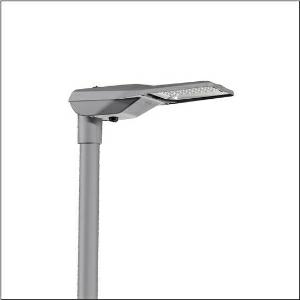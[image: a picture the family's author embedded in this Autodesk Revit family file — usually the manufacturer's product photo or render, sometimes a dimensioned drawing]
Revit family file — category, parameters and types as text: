
# Revit family: streetlight_sl_21_iq_mini___st1_0ab_5xe2m31y08gb_c9fc
name_source: partatom
category: Lighting Fixtures
units: mm (PartAtom-declared; Revit-internal decimal feet)

## family parameters
Cut with Voids When Loaded = No
Host = Face
Light Source = No
Part Type = Normal
Room Calculation Point = No
Round Connector Dimension = Use Diameter
Shared = No

## types (1)
- --- (1 x LED, 5270 lm, 39.8 W, 3000K)
    Apparent Load = 40 VA
    CIE Flux Codes = 38 73 97 100 100
    Color Rendering = 70
    Color Temperature = 3000K
    Default Elevation = 1800 mm
    Description = Streetlight SL 21 iQ mini, mast luminaire, primary light control with lens, of PMMA, primary optical cover: cover, of toughened safety glass, transparent, light distribution: ST1.0aB, light emission: direct distribution, primary light characteristic: asymmetric, installation type: post-top, side-entry, LED, High Power LED, rated luminous flux: 5.270lm, luminous efficacy: 132lm/W, light colour: 730, colour temperature: 3000K, control gear: iQ-Street Remote, D4i with power reduction, control: pre-setting: logarithmic dimming characteristic, Street-Remote, Auto-Match, Temp-Guard, Lumen-Switch, Night-Set, Smart-Wire, Light-Fading, Desk-Remote (wireless, voltage-free reading and setting of iQ features in the workshop via application-optimized NFC function/RFID function), optimised constant luminous flux control (CLO 2.0), mains connection: 220..240V, AC, 50/60Hz, start of lifetime: 40W, end of service life: 41W, reduction: 18W, luminaire housing, of diecast aluminium, powder-coated, Siteco® metallic grey (DB 702S), corrosivity category C5 mid according to DIN EN ISO 12944, please order mast flange separately, inclination adjustable: 0°, 5°, 10°, 15°, sealing non-destructively replaceable, multi-level sealing system, length: 628mm, width: 235mm, height: 110mm, mast flange for spigot size: 42mm (side-entry): 5XC10008XM4, 60/48mm (side-entry/post-top): 5XC10108XM2, 76/60mm (side-entry/post-top): 5XC10108XM1, mounting height: 4..8m, Smart Interface below and above, protection rating (complete): IP66, insulation class (complete): insulation class II (safety insulation), certification: CE, ENEC, ENEC+, VDE, impact resistance: IK10, permissible operating ambient temperature for outdoor applications: -40..+50°C, standard-compliant lighting for roads and squares, packaging unit: 1 piece

Light Distribution: ST1.0aB
    Height = 110 mm
    Lamp = 1 x LED
    Lamp Light Flux = 5270 lm
    Lamp Power = 39.8 W
    Lamp count = 1
    Length = 625 mm
    Luminous efficacy = 132 lm/W
    Manufacturer = Siteco
    ModVariant = No
    Model = 5XE2M31Y08GB
    Number of Poles = 1
    OnlyDefault = Yes
    Power Factor = 1
    Product Name = Streetlight SL 21 iQ mini | ST1.0aB
    Product group = mast luminaire | pylon top
    ProductGroupID = 6100
    Protection Class = Protection class II
    Protection Degree = IP 66
    RLX_Detail_Level = 1
    RLX_Emergency_Light_Flux = 0 lm
    RLX_Emergency_Type = 0
    RLX_Emergency_Type_DB = No
    RlxData = <blob elided: 26793 chars, md5=81b2145c>
    Socket = socket
    Standby Power = 0 W
    System Light Flux = 5270 lm
    System Power = 40 W
    Type Comments = factory setting: luminous flux: 100 % | dim-lin: 254 | 800 mA
    Type Image = l_1003514.jpg
    URL = http://relux.com
    VarID = @adj_112438
    Voltage = 0 V
    Weight = 0.00 kg
    Width = 234 mm

## geometry (parser evidence)
native form markers: Blend x4, Sweep x9
no freeform markers — native parametric forms only
